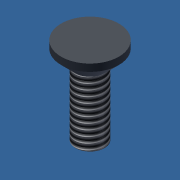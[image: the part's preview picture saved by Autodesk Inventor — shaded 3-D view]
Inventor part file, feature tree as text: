
AUTODESK INVENTOR PART (.ipt)
format: ipt  version: 2016 (Build 200138000, 138)  size: 107,008 bytes
history: native  units: mm
features: extrude x3, sketch x3, other x1, chamfer x1, thread x1
ambient origin geometry x1: Origin
bodies: Body1 (feature_tree)
feature tree (9):
  other  "ソリッド1"
  extrude  "押し出し1"  Depth=2.0mm
  extrude  "押し出し2"  Depth=4.0mm TaperAngle=0.0deg
  chamfer  "面取り1"  Distance=4.0mm
  thread  "ねじ1"
  extrude  "押し出し3"  Depth=1.5mm TaperAngle=0.0deg
  sketch  "スケッチ1"
  sketch  "スケッチ2"
  sketch  "スケッチ3"
